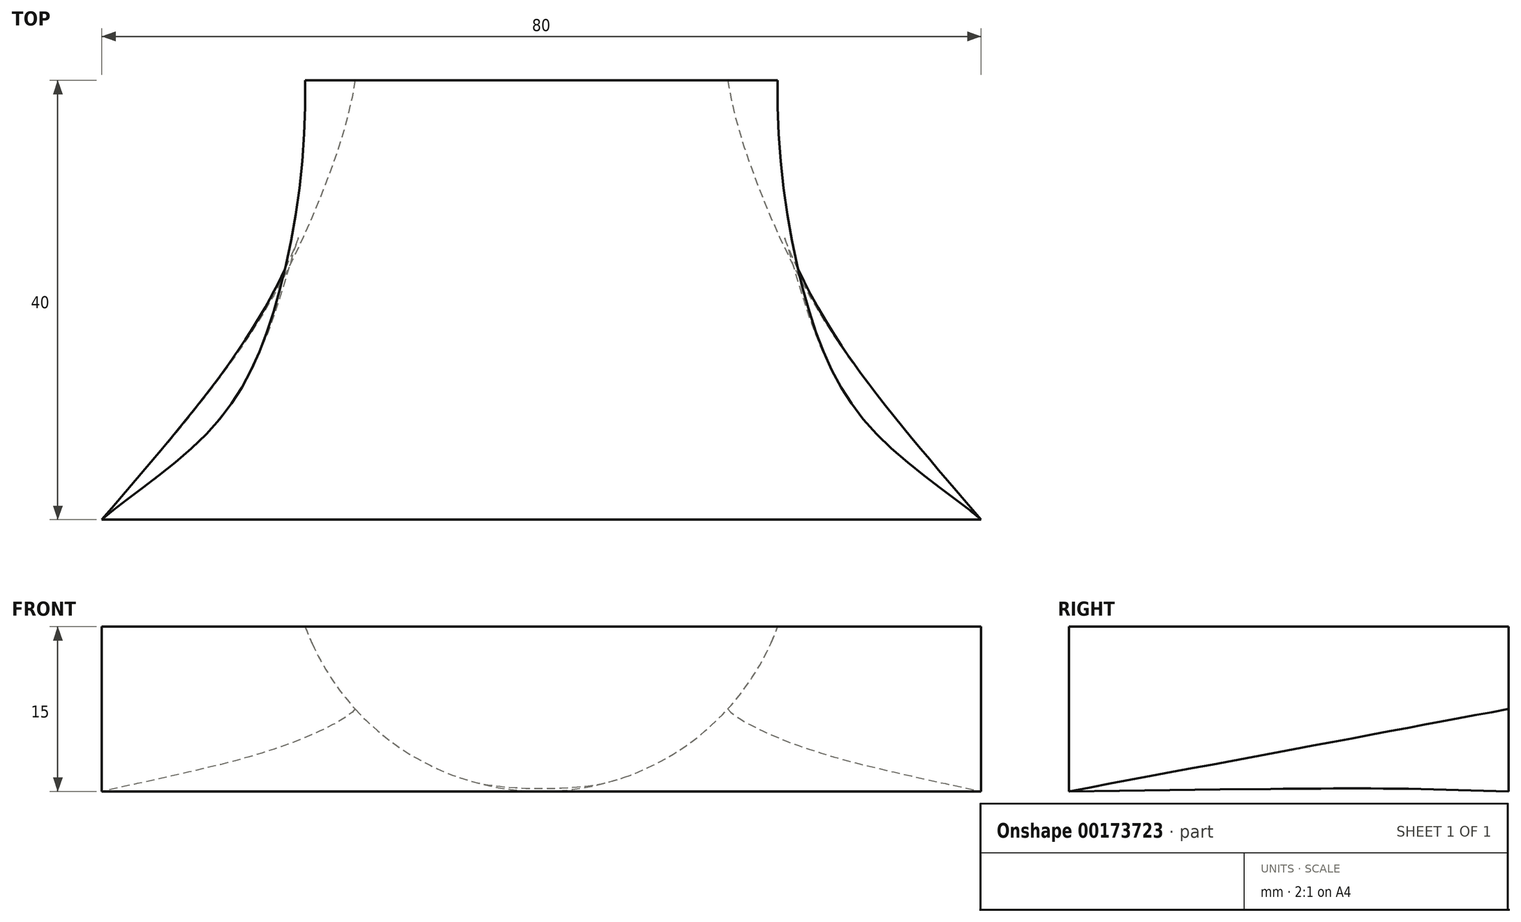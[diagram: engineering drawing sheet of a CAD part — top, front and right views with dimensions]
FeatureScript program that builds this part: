
annotation { "Feature Type Name" : "Feature", "Feature Type Description" : "" }
export const myFeature = defineFeature(function(context is Context, id is Id, definition is map)
    precondition{}
    {
        {
            var Q0;
            Q0=qCreatedBy(makeId("Front.planeOp"),FACE);
            cPlane(context, id + "F0", {"entities" : qUnion([Q0]), "cplaneType" : CPlaneType.OFFSET, "offset" : 40 * mm, "width" : 150 * mm, "height" : 150 * mm});
        }
        {
            var Q0;
            Q0=qCreatedBy(makeId("Front.planeOp"),FACE);
            var sketch = newSketch(context, id + "F1", { "sketchPlane" : qUnion([Q0])});
            skLineSegment(sketch, "E0", {"start": v(-21.5, 7.5) * mm, "end": v(21.5, 7.5) * mm});
            skArc(sketch, "E1", {"start": v(-21.5, 7.5) * mm, "mid": v(0, -7.5) * mm, "end": v(21.5, 7.5) * mm});
            skPoint(sketch, "E2", {"position": v(0, -7.5) * mm});
            skSolve(sketch);
        }
        {
            var Q0;
            Q0=qCreatedBy(id+"F0.planeOp",FACE);
            var sketch = newSketch(context, id + "F2", { "sketchPlane" : qUnion([Q0])});
            skLineSegment(sketch, "E3.bottom", {"start": v(40, -7.5) * mm, "end": v(-40, -7.5) * mm});
            skLineSegment(sketch, "E3.top", {"start": v(40, 7.5) * mm, "end": v(-40, 7.5) * mm});
            skLineSegment(sketch, "E3.left", {"start": v(40, -7.5) * mm, "end": v(40, 7.5) * mm});
            skLineSegment(sketch, "E3.right", {"start": v(-40, -7.5) * mm, "end": v(-40, 7.5) * mm});
            skPoint(sketch, "E3.middle", {"position": v(0, 0) * mm});
            skSolve(sketch);
        }
        {
            var Q0;
            Q0=sQuery(id+"F2.wireOp",VERTEX,"E3.top.end");
            var Q1;
            Q1=sQuery(id+"F2.wireOp",VERTEX,"E3.left.end");
            var Q2;
            Q2=sQuery(id+"F1.wireOp",VERTEX,"E1.end");
            cPlane(context, id + "F3", {"entities" : qUnion([Q0, Q1, Q2]), "cplaneType" : CPlaneType.THREE_POINT, "offset" : 25 * mm, "width" : 150 * mm, "height" : 150 * mm});
        }
        {
            var Q0;
            Q0=qCreatedBy(id+"F3.planeOp",FACE);
            var sketch = newSketch(context, id + "F4", { "sketchPlane" : qUnion([Q0])});
            skFitSpline(sketch, "E4", {"points": [v(-40, 40) * mm, v(-30.74, 32.45) * mm, v(-24.45, 21.32) * mm, v(-21.5, 0) * mm], "startDerivative": vector(20.72, -18.05) * mm, "endDerivative": vector(-1.38, -55.56) * mm});
            skFitSpline(sketch, "E5.MirrorCS", {"points": [v(40, 40) * mm, v(30.74, 32.45) * mm, v(24.45, 21.32) * mm, v(21.5, 0) * mm], "startDerivative": vector(-20.72, -18.05) * mm, "endDerivative": vector(1.38, -55.56) * mm});
            skSolve(sketch);
        }
        {
            var Q0;
            Q0=qCreatedBy(makeId("Origin.pointOp"),VERTEX);
            var Q1;
            Q1=sQuery(id+"F2.wireOp",VERTEX,"E3.right.start");
            var Q2;
            Q2=sQuery(id+"F2.wireOp",VERTEX,"E3.left.start");
            cPlane(context, id + "F5", {"entities" : qUnion([Q0, Q1, Q2]), "cplaneType" : CPlaneType.THREE_POINT, "offset" : 25 * mm, "width" : 150 * mm, "height" : 150 * mm});
        }
        {
            var Q0;
            Q0=qCreatedBy(id+"F5.planeOp",FACE);
            var sketch = newSketch(context, id + "F6", { "sketchPlane" : qUnion([Q0])});
            skFitSpline(sketch, "E6", {"points": [v(-16.95, 0) * mm, v(-19.7, 9.72) * mm, v(-26.4, 23.34) * mm, v(-40, 40.7) * mm], "startDerivative": vector(-5.65, 36.5) * mm, "endDerivative": vector(-37.28, 44.05) * mm});
            skFitSpline(sketch, "E7.MirrorCS", {"points": [v(16.95, 0) * mm, v(19.7, 9.72) * mm, v(26.4, 23.34) * mm, v(40, 40.7) * mm], "startDerivative": vector(5.65, 36.5) * mm, "endDerivative": vector(37.28, 44.05) * mm});
            skSolve(sketch);
        }
        {
            var Q0;
            Q0=makeQuery(id+"F1.imprint","IMPRINT",FACE,{"disambiguationData":[TD([[makeQuery(id+"F1.imprint","IMPRINT",EDGE,{"derivedFrom":sQuery(id+"F1.wireOp",EDGE,"E0")}),-1.0]])]});
            var Q1;
            Q1=makeQuery(id+"F2.imprint","IMPRINT",FACE,{"disambiguationData":[TD([[makeQuery(id+"F2.imprint","IMPRINT",EDGE,{"derivedFrom":sQuery(id+"F2.wireOp",EDGE,"E3.bottom")}),-1.0]])]});
            var Q2;
            Q2=sQuery(id+"F4.wireOp",EDGE,"E4");
            var Q3;
            Q3=sQuery(id+"F4.wireOp",EDGE,"E5.MirrorCS");
            var Q4;
            Q4=sQuery(id+"F6.wireOp",EDGE,"E6");
            var Q5;
            Q5=sQuery(id+"F6.wireOp",EDGE,"E7.MirrorCS");
            loft(context, id + "F7", {"addGuides" : true, "sheetProfilesArray" : [{ "sheetProfileEntities" : qUnion([Q0]) }, { "sheetProfileEntities" : qUnion([Q1]) }], "guidesArray" : [{ "guideEntities" : qUnion([Q2]), "guideDerivativeType" : LoftGuideDerivativeType.DEFAULT, "guideDerivativeMagnitude" : 1 }, { "guideEntities" : qUnion([Q3]), "guideDerivativeType" : LoftGuideDerivativeType.DEFAULT, "guideDerivativeMagnitude" : 1 }, { "guideEntities" : qUnion([Q4]), "guideDerivativeType" : LoftGuideDerivativeType.DEFAULT, "guideDerivativeMagnitude" : 1 }, { "guideEntities" : qUnion([Q5]), "guideDerivativeType" : LoftGuideDerivativeType.DEFAULT, "guideDerivativeMagnitude" : 1 }]});
        }
    });
